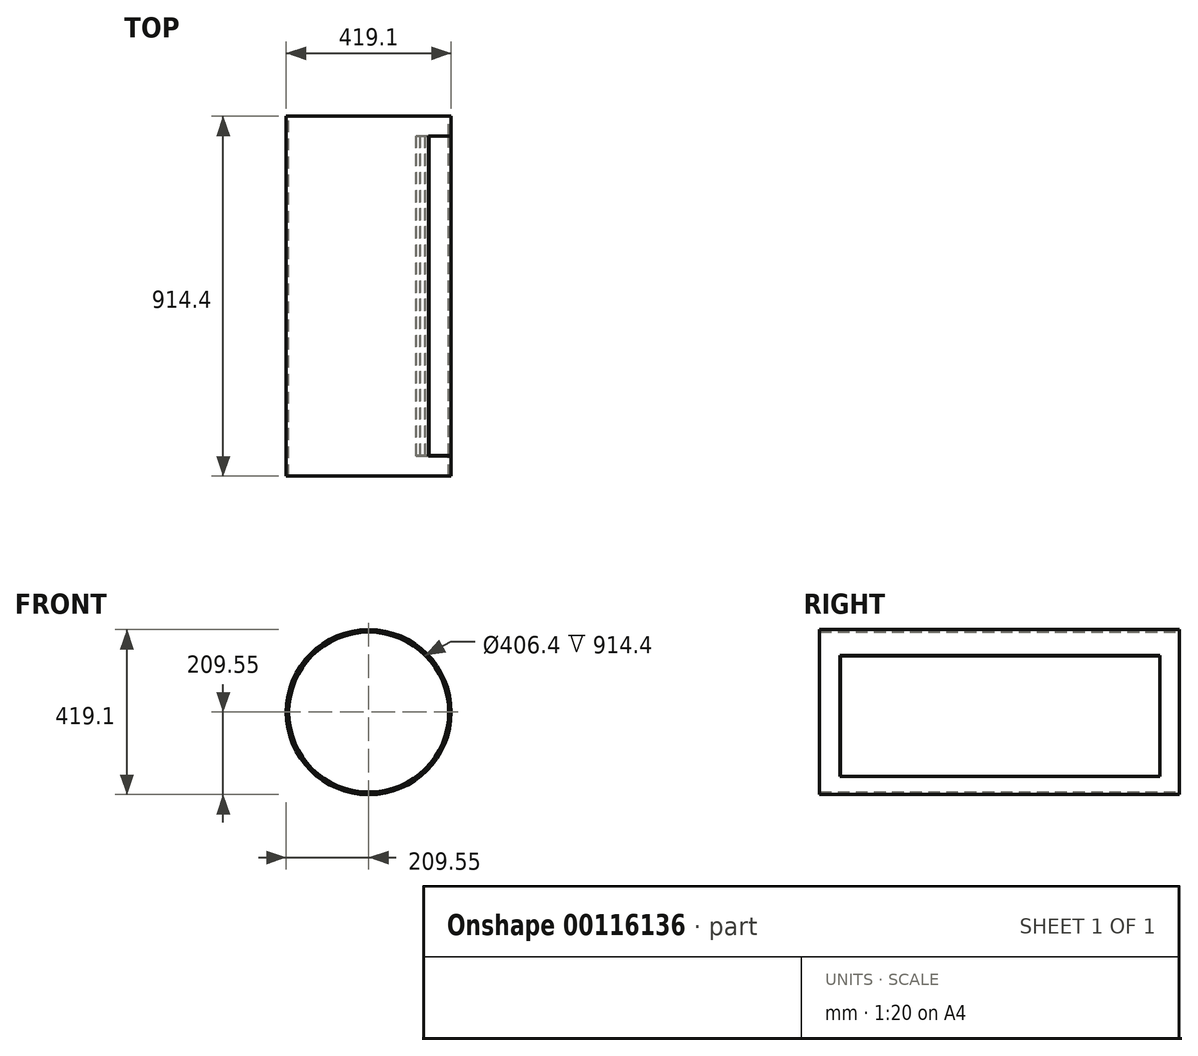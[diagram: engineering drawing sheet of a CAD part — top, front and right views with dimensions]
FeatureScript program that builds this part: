
annotation { "Feature Type Name" : "Feature", "Feature Type Description" : "" }
export const myFeature = defineFeature(function(context is Context, id is Id, definition is map)
    precondition{}
    {
        {
            var Q0;
            Q0=qCreatedBy(makeId("Front.planeOp"),FACE);
            var sketch = newSketch(context, id + "F0", { "sketchPlane" : qUnion([Q0])});
            skCircle(sketch, "E0", {"center": v(0, 0) * mm, "radius": 209.55 * mm});
            skSolve(sketch);
        }
        {
            var Q0;
            Q0=makeQuery(id+"F0.imprint","IMPRINT",FACE,{"disambiguationData":[TD([[makeQuery(id+"F0.imprint","IMPRINT",EDGE,{"derivedFrom":sQuery(id+"F0.wireOp",EDGE,"E0")}),1.0]])]});
            extrude(context, id + "F1", {"entities" : qUnion([Q0]), "depth" : 914.4 * mm});
        }
        {
            var Q0;
            Q0=makeQuery(id+"F1.opExtrude","CAP_FACE",FACE,{"disambiguationData":[OSD([sQuery(id+"F0.wireOp",EDGE,"E0")])],"isStart":false});
            var Q1;
            Q1=makeQuery(id+"F1.opExtrude","CAP_FACE",FACE,{"disambiguationData":[OSD([sQuery(id+"F0.wireOp",EDGE,"E0")])],"isStart":true});
            shell(context, id + "F2", {"entities" : qUnion([Q0, Q1]), "thickness" : 6.35 * mm});
        }
        {
            var Q0;
            Q0=qCreatedBy(makeId("Right.planeOp"),FACE);
            var sketch = newSketch(context, id + "F3", { "sketchPlane" : qUnion([Q0])});
            skLineSegment(sketch, "E1.bottom", {"start": v(-861.39, 142.52) * mm, "end": v(-50.38, 142.52) * mm});
            skLineSegment(sketch, "E1.top", {"start": v(-861.39, -163.3) * mm, "end": v(-50.38, -163.3) * mm});
            skLineSegment(sketch, "E1.left", {"start": v(-861.39, 142.52) * mm, "end": v(-861.39, -163.3) * mm});
            skLineSegment(sketch, "E1.right", {"start": v(-50.38, 142.52) * mm, "end": v(-50.38, -163.3) * mm});
            skLineSegment(sketch, "E2.bottom", {"start": v(-49.87, -163.78) * mm, "end": v(-862.7, -163.78) * mm});
            skLineSegment(sketch, "E2.top", {"start": v(-49.87, 143.9) * mm, "end": v(-862.7, 143.9) * mm});
            skLineSegment(sketch, "E2.left", {"start": v(-49.87, -163.78) * mm, "end": v(-49.87, 143.9) * mm});
            skLineSegment(sketch, "E2.right", {"start": v(-862.7, -163.78) * mm, "end": v(-862.7, 143.9) * mm});
            skSolve(sketch);
        }
        {
            var Q0;
            Q0 = qSketchRegion(id + "F3", true);
            extrude(context, id + "F4", {"entities" : qUnion([Q0]), "operationType" : NewBodyOperationType.REMOVE, "depth" : 447 * mm});
        }
    });
